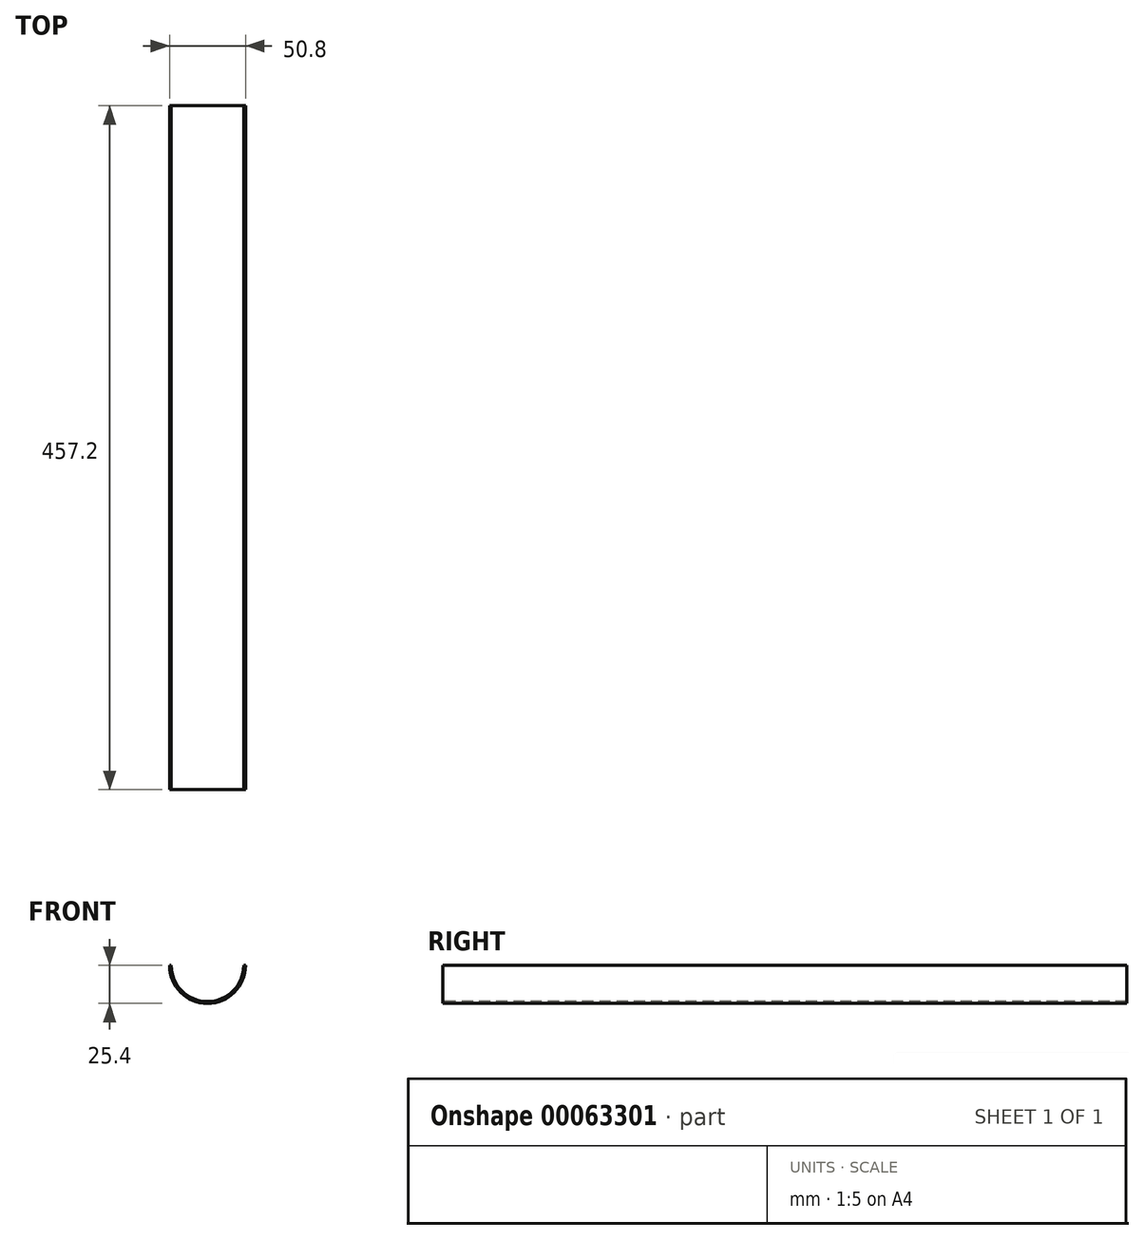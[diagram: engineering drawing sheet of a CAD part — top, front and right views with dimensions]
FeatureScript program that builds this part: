
annotation { "Feature Type Name" : "Feature", "Feature Type Description" : "" }
export const myFeature = defineFeature(function(context is Context, id is Id, definition is map)
    precondition{}
    {
        {
            var Q0;
            Q0=qCreatedBy(makeId("Front.planeOp"),FACE);
            var sketch = newSketch(context, id + "F0", { "sketchPlane" : qUnion([Q0])});
            skArc(sketch, "E0", {"start": v(-25.4, 0) * mm, "mid": v(0, -25.4) * mm, "end": v(25.4, 0) * mm});
            skLineSegment(sketch, "E1", {"start": v(0, 0) * mm, "end": v(25.4, 0) * mm});
            skLineSegment(sketch, "E2", {"start": v(0, 0) * mm, "end": v(-25.4, 0) * mm});
            skSolve(sketch);
        }
        {
            var Q0;
            Q0=makeQuery(id+"F0.imprint","IMPRINT",FACE,{"disambiguationData":[TD([[makeQuery(id+"F0.imprint","IMPRINT",EDGE,{"derivedFrom":sQuery(id+"F0.wireOp",EDGE,"E0")}),1.0]])]});
            extrude(context, id + "F1", {"entities" : qUnion([Q0]), "depth" : 457.2 * mm});
        }
        {
            var Q0;
            Q0=makeQuery(id+"F1.opExtrude","CAP_FACE",FACE,{"disambiguationData":[OSD([sQuery(id+"F0.wireOp",EDGE,"E0"),sQuery(id+"F0.wireOp",EDGE,"E1"),sQuery(id+"F0.wireOp",EDGE,"E2")])],"isStart":false});
            var sketch = newSketch(context, id + "F2", { "sketchPlane" : qUnion([Q0])});
            skArc(sketch, "E3", {"start": v(-24.13, 0) * mm, "mid": v(0, -24.13) * mm, "end": v(24.13, 0) * mm});
            skLineSegment(sketch, "E4", {"start": v(-24.13, 0) * mm, "end": v(19.49, 0) * mm});
            skLineSegment(sketch, "E5", {"start": v(19.49, 0) * mm, "end": v(25.4, 0) * mm});
            skSolve(sketch);
        }
        {
            var Q0;
            Q0 = qSketchRegion(id + "F2", true);
            extrude(context, id + "F3", {"entities" : qUnion([Q0]), "operationType" : NewBodyOperationType.REMOVE, "endBound" : BoundingType.THROUGH_ALL, "oppositeDirection" : true, "depth" : 25.4 * mm});
        }
    });
